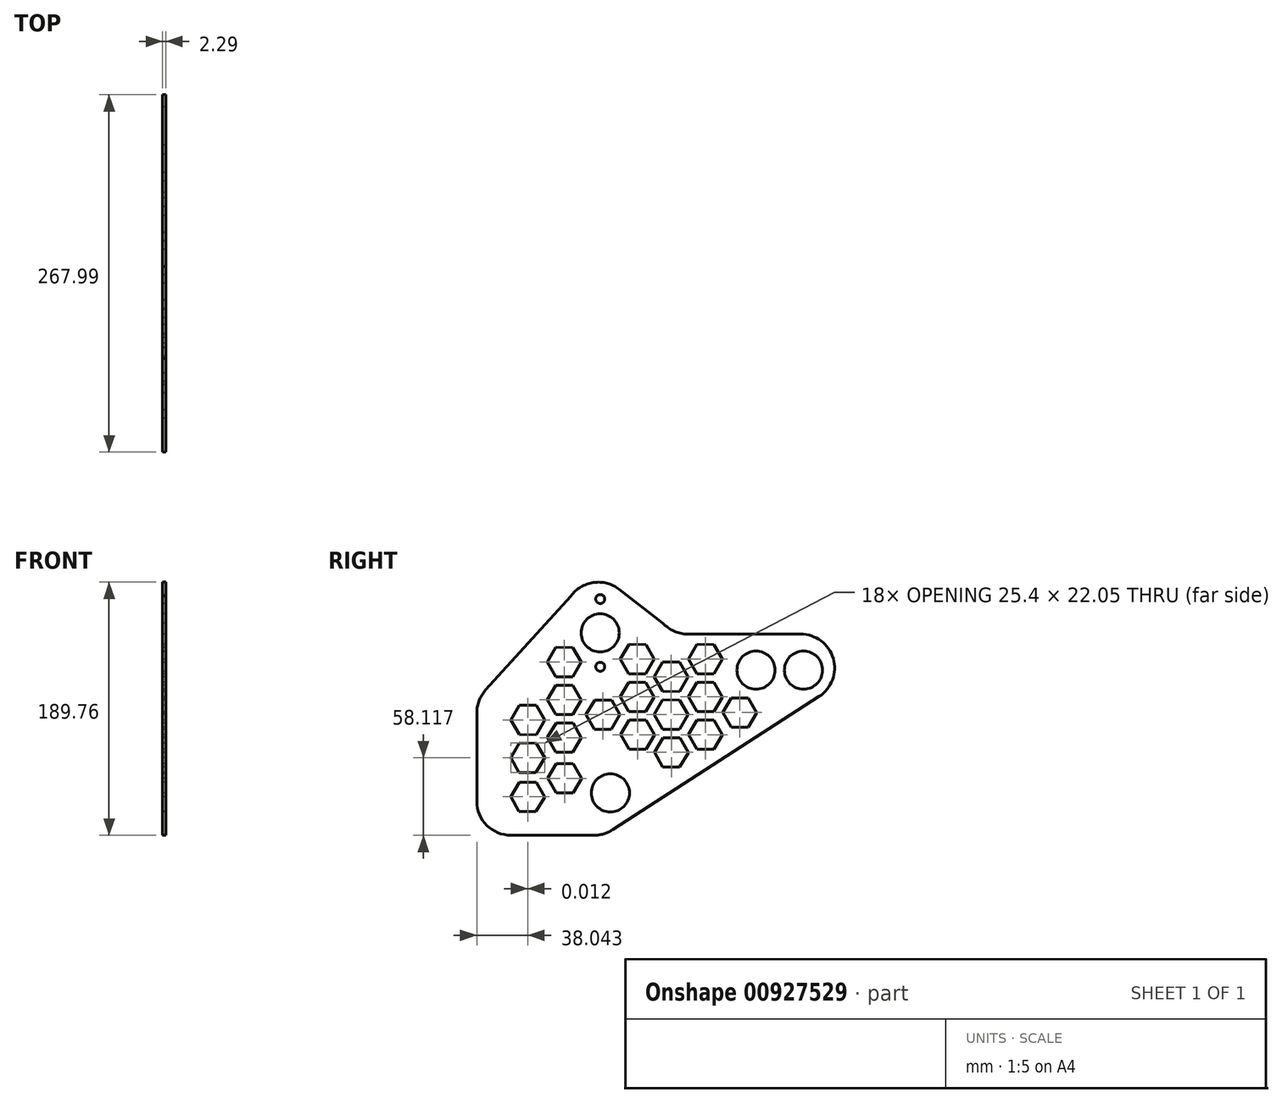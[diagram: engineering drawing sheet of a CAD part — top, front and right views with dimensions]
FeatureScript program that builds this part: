
annotation { "Feature Type Name" : "Feature", "Feature Type Description" : "" }
export const myFeature = defineFeature(function(context is Context, id is Id, definition is map)
    precondition{}
    {
        {
            var Q0;
            Q0=qCreatedBy(makeId("Right.planeOp"),FACE);
            var sketch = newSketch(context, id + "F0", { "sketchPlane" : qUnion([Q0])});
            skCircle(sketch, "E0", {"center": v(115.22, 53.73) * mm, "radius": 14.29 * mm});
            skCircle(sketch, "E1", {"center": v(79.66, 53.73) * mm, "radius": 14.29 * mm});
            skCircle(sketch, "E2", {"center": v(-37.05, 81.65) * mm, "radius": 14.29 * mm});
            skCircle(sketch, "E3", {"center": v(-29.41, -38.35) * mm, "radius": 14.29 * mm});
            skLineSegment(sketch, "E4", {"start": v(179.97, -95.5) * mm, "end": v(-160.98, -95.5) * mm});
            skCircle(sketch, "E5", {"center": v(-37.05, 107.05) * mm, "radius": 3.37 * mm});
            skCircle(sketch, "E6", {"center": v(-37.05, 56.25) * mm, "radius": 3.37 * mm});
            skLineSegment(sketch, "E7", {"start": v(-27.9, -66.03) * mm, "end": v(126.93, 33.98) * mm});
            skLineSegment(sketch, "E8", {"start": v(28.64, 80.72) * mm, "end": v(113.15, 80.72) * mm});
            skPoint(sketch, "E9.visualSharp", {"position": v(199.28, 80.72) * mm});
            skArc(sketch, "E9.filletArc", {"start": v(126.93, 33.98) * mm, "mid": v(137.51, 62.5) * mm, "end": v(113.15, 80.72) * mm});
            skPoint(sketch, "E10.visualSharp", {"position": v(17.39, 80.72) * mm});
            skArc(sketch, "E10.filletArc", {"start": v(9.83, 89.05) * mm, "mid": v(18.35, 82.9) * mm, "end": v(28.64, 80.72) * mm});
            skPoint(sketch, "E11.visualSharp", {"position": v(-180.09, -142.09) * mm});
            skPoint(sketch, "E12.visualSharp", {"position": v(-115.75, -108.8) * mm});
            skPoint(sketch, "E13.visualSharp", {"position": v(-31.87, -68.6) * mm});
            skCircle(sketch, "E14.cCircle", {"center": v(41.75, 62) * mm, "radius": 11 * mm, "construction": true});
            skLineSegment(sketch, "E14.0", {"start": v(35.35, 51.04) * mm, "end": v(29.05, 62.07) * mm});
            skLineSegment(sketch, "E14.1", {"start": v(29.05, 62.07) * mm, "end": v(35.45, 73.04) * mm});
            skLineSegment(sketch, "E14.2", {"start": v(35.45, 73.04) * mm, "end": v(48.15, 72.98) * mm});
            skLineSegment(sketch, "E14.3", {"start": v(48.15, 72.98) * mm, "end": v(54.45, 61.95) * mm});
            skLineSegment(sketch, "E14.4", {"start": v(54.45, 61.95) * mm, "end": v(48.05, 50.98) * mm});
            skLineSegment(sketch, "E14.5", {"start": v(48.05, 50.98) * mm, "end": v(35.35, 51.04) * mm});
            skPoint(sketch, "E14.0.midPoint", {"position": v(32.2, 56.55) * mm});
            skCircle(sketch, "E15.cCircle", {"center": v(41.69, 33.66) * mm, "radius": 11 * mm, "construction": true});
            skLineSegment(sketch, "E15.0", {"start": v(35.29, 22.7) * mm, "end": v(28.99, 33.72) * mm});
            skLineSegment(sketch, "E15.1", {"start": v(28.99, 33.72) * mm, "end": v(35.39, 44.69) * mm});
            skLineSegment(sketch, "E15.2", {"start": v(35.39, 44.69) * mm, "end": v(48.09, 44.63) * mm});
            skLineSegment(sketch, "E15.3", {"start": v(48.09, 44.63) * mm, "end": v(54.39, 33.6) * mm});
            skLineSegment(sketch, "E15.4", {"start": v(54.39, 33.6) * mm, "end": v(47.99, 22.64) * mm});
            skLineSegment(sketch, "E15.5", {"start": v(47.99, 22.64) * mm, "end": v(35.29, 22.7) * mm});
            skPoint(sketch, "E15.0.midPoint", {"position": v(32.14, 28.2) * mm});
            skCircle(sketch, "E16.cCircle", {"center": v(41.84, 5.32) * mm, "radius": 11 * mm, "construction": true});
            skLineSegment(sketch, "E16.0", {"start": v(35.45, -5.65) * mm, "end": v(29.14, 5.37) * mm});
            skLineSegment(sketch, "E16.1", {"start": v(29.14, 5.37) * mm, "end": v(35.54, 16.34) * mm});
            skLineSegment(sketch, "E16.2", {"start": v(35.54, 16.34) * mm, "end": v(48.24, 16.29) * mm});
            skLineSegment(sketch, "E16.3", {"start": v(48.24, 16.29) * mm, "end": v(54.54, 5.26) * mm});
            skLineSegment(sketch, "E16.4", {"start": v(54.54, 5.26) * mm, "end": v(48.15, -5.71) * mm});
            skLineSegment(sketch, "E16.5", {"start": v(48.15, -5.71) * mm, "end": v(35.45, -5.65) * mm});
            skPoint(sketch, "E16.0.midPoint", {"position": v(32.3, -0.14) * mm});
            skCircle(sketch, "E17.cCircle", {"center": v(16.13, 48.74) * mm, "radius": 11 * mm, "construction": true});
            skLineSegment(sketch, "E17.0", {"start": v(9.73, 37.77) * mm, "end": v(3.43, 48.8) * mm});
            skLineSegment(sketch, "E17.1", {"start": v(3.43, 48.8) * mm, "end": v(9.83, 59.77) * mm});
            skLineSegment(sketch, "E17.2", {"start": v(9.83, 59.77) * mm, "end": v(22.53, 59.71) * mm});
            skLineSegment(sketch, "E17.3", {"start": v(22.53, 59.71) * mm, "end": v(28.83, 48.69) * mm});
            skLineSegment(sketch, "E17.4", {"start": v(28.83, 48.69) * mm, "end": v(22.43, 37.72) * mm});
            skLineSegment(sketch, "E17.5", {"start": v(22.43, 37.72) * mm, "end": v(9.73, 37.77) * mm});
            skPoint(sketch, "E17.0.midPoint", {"position": v(6.58, 43.29) * mm});
            skCircle(sketch, "E18.cCircle", {"center": v(16.07, 20.4) * mm, "radius": 11 * mm, "construction": true});
            skLineSegment(sketch, "E18.0", {"start": v(9.67, 9.43) * mm, "end": v(3.37, 20.45) * mm});
            skLineSegment(sketch, "E18.1", {"start": v(3.37, 20.45) * mm, "end": v(9.77, 31.42) * mm});
            skLineSegment(sketch, "E18.2", {"start": v(9.77, 31.42) * mm, "end": v(22.47, 31.37) * mm});
            skLineSegment(sketch, "E18.3", {"start": v(22.47, 31.37) * mm, "end": v(28.77, 20.34) * mm});
            skLineSegment(sketch, "E18.4", {"start": v(28.77, 20.34) * mm, "end": v(22.37, 9.37) * mm});
            skLineSegment(sketch, "E18.5", {"start": v(22.37, 9.37) * mm, "end": v(9.67, 9.43) * mm});
            skPoint(sketch, "E18.0.midPoint", {"position": v(6.52, 14.94) * mm});
            skCircle(sketch, "E19.cCircle", {"center": v(16.23, -7.95) * mm, "radius": 11 * mm, "construction": true});
            skLineSegment(sketch, "E19.0", {"start": v(9.83, -18.92) * mm, "end": v(3.53, -7.9) * mm});
            skLineSegment(sketch, "E19.1", {"start": v(3.53, -7.9) * mm, "end": v(9.92, 3.08) * mm});
            skLineSegment(sketch, "E19.2", {"start": v(9.92, 3.08) * mm, "end": v(22.62, 3.02) * mm});
            skLineSegment(sketch, "E19.3", {"start": v(22.62, 3.02) * mm, "end": v(28.93, -8) * mm});
            skLineSegment(sketch, "E19.4", {"start": v(28.93, -8) * mm, "end": v(22.53, -18.98) * mm});
            skLineSegment(sketch, "E19.5", {"start": v(22.53, -18.98) * mm, "end": v(9.83, -18.92) * mm});
            skPoint(sketch, "E19.0.midPoint", {"position": v(6.68, -13.4) * mm});
            skCircle(sketch, "E20.cCircle", {"center": v(-9.22, 62) * mm, "radius": 11 * mm, "construction": true});
            skLineSegment(sketch, "E20.0", {"start": v(-15.62, 51.04) * mm, "end": v(-21.92, 62.07) * mm});
            skLineSegment(sketch, "E20.1", {"start": v(-21.92, 62.07) * mm, "end": v(-15.52, 73.04) * mm});
            skLineSegment(sketch, "E20.2", {"start": v(-15.52, 73.04) * mm, "end": v(-2.82, 72.98) * mm});
            skLineSegment(sketch, "E20.3", {"start": v(-2.82, 72.98) * mm, "end": v(3.48, 61.95) * mm});
            skLineSegment(sketch, "E20.4", {"start": v(3.48, 61.95) * mm, "end": v(-2.92, 50.98) * mm});
            skLineSegment(sketch, "E20.5", {"start": v(-2.92, 50.98) * mm, "end": v(-15.62, 51.04) * mm});
            skPoint(sketch, "E20.0.midPoint", {"position": v(-18.77, 56.55) * mm});
            skCircle(sketch, "E21.cCircle", {"center": v(-9.27, 33.66) * mm, "radius": 11 * mm, "construction": true});
            skLineSegment(sketch, "E21.0", {"start": v(-15.67, 22.7) * mm, "end": v(-21.97, 33.72) * mm});
            skLineSegment(sketch, "E21.1", {"start": v(-21.97, 33.72) * mm, "end": v(-15.58, 44.69) * mm});
            skLineSegment(sketch, "E21.2", {"start": v(-15.58, 44.69) * mm, "end": v(-2.88, 44.63) * mm});
            skLineSegment(sketch, "E21.3", {"start": v(-2.88, 44.63) * mm, "end": v(3.43, 33.6) * mm});
            skLineSegment(sketch, "E21.4", {"start": v(3.43, 33.6) * mm, "end": v(-2.97, 22.64) * mm});
            skLineSegment(sketch, "E21.5", {"start": v(-2.97, 22.64) * mm, "end": v(-15.67, 22.7) * mm});
            skPoint(sketch, "E21.0.midPoint", {"position": v(-18.82, 28.2) * mm});
            skCircle(sketch, "E22.cCircle", {"center": v(-9.12, 5.32) * mm, "radius": 11 * mm, "construction": true});
            skLineSegment(sketch, "E22.0", {"start": v(-15.52, -5.65) * mm, "end": v(-21.82, 5.37) * mm});
            skLineSegment(sketch, "E22.1", {"start": v(-21.82, 5.37) * mm, "end": v(-15.42, 16.34) * mm});
            skLineSegment(sketch, "E22.2", {"start": v(-15.42, 16.34) * mm, "end": v(-2.72, 16.29) * mm});
            skLineSegment(sketch, "E22.3", {"start": v(-2.72, 16.29) * mm, "end": v(3.58, 5.26) * mm});
            skLineSegment(sketch, "E22.4", {"start": v(3.58, 5.26) * mm, "end": v(-2.82, -5.71) * mm});
            skLineSegment(sketch, "E22.5", {"start": v(-2.82, -5.71) * mm, "end": v(-15.52, -5.65) * mm});
            skPoint(sketch, "E22.0.midPoint", {"position": v(-18.67, -0.14) * mm});
            skCircle(sketch, "E23.cCircle", {"center": v(-34.94, 20.34) * mm, "radius": 11 * mm, "construction": true});
            skLineSegment(sketch, "E23.0", {"start": v(-41.34, 9.37) * mm, "end": v(-47.64, 20.4) * mm});
            skLineSegment(sketch, "E23.1", {"start": v(-47.64, 20.4) * mm, "end": v(-41.25, 31.37) * mm});
            skLineSegment(sketch, "E23.2", {"start": v(-41.25, 31.37) * mm, "end": v(-28.55, 31.31) * mm});
            skLineSegment(sketch, "E23.3", {"start": v(-28.55, 31.31) * mm, "end": v(-22.24, 20.28) * mm});
            skLineSegment(sketch, "E23.4", {"start": v(-22.24, 20.28) * mm, "end": v(-28.64, 9.31) * mm});
            skLineSegment(sketch, "E23.5", {"start": v(-28.64, 9.31) * mm, "end": v(-41.34, 9.37) * mm});
            skPoint(sketch, "E23.0.midPoint", {"position": v(-44.5, 14.88) * mm});
            skCircle(sketch, "E24.cCircle", {"center": v(-63.94, 59.77) * mm, "radius": 11 * mm, "construction": true});
            skLineSegment(sketch, "E24.0", {"start": v(-70.34, 48.8) * mm, "end": v(-76.64, 59.83) * mm});
            skLineSegment(sketch, "E24.1", {"start": v(-76.64, 59.83) * mm, "end": v(-70.24, 70.8) * mm});
            skLineSegment(sketch, "E24.2", {"start": v(-70.24, 70.8) * mm, "end": v(-57.54, 70.74) * mm});
            skLineSegment(sketch, "E24.3", {"start": v(-57.54, 70.74) * mm, "end": v(-51.24, 59.71) * mm});
            skLineSegment(sketch, "E24.4", {"start": v(-51.24, 59.71) * mm, "end": v(-57.64, 48.74) * mm});
            skLineSegment(sketch, "E24.5", {"start": v(-57.64, 48.74) * mm, "end": v(-70.34, 48.8) * mm});
            skPoint(sketch, "E24.0.midPoint", {"position": v(-73.5, 54.31) * mm});
            skCircle(sketch, "E25.cCircle", {"center": v(-64, 31.42) * mm, "radius": 11 * mm, "construction": true});
            skLineSegment(sketch, "E25.0", {"start": v(-70.4, 20.45) * mm, "end": v(-76.7, 31.48) * mm});
            skLineSegment(sketch, "E25.1", {"start": v(-76.7, 31.48) * mm, "end": v(-70.3, 42.45) * mm});
            skLineSegment(sketch, "E25.2", {"start": v(-70.3, 42.45) * mm, "end": v(-57.6, 42.4) * mm});
            skLineSegment(sketch, "E25.3", {"start": v(-57.6, 42.4) * mm, "end": v(-51.3, 31.37) * mm});
            skLineSegment(sketch, "E25.4", {"start": v(-51.3, 31.37) * mm, "end": v(-57.7, 20.4) * mm});
            skLineSegment(sketch, "E25.5", {"start": v(-57.7, 20.4) * mm, "end": v(-70.4, 20.45) * mm});
            skPoint(sketch, "E25.0.midPoint", {"position": v(-73.55, 25.97) * mm});
            skCircle(sketch, "E26.cCircle", {"center": v(-63.84, 3.08) * mm, "radius": 11 * mm, "construction": true});
            skLineSegment(sketch, "E26.0", {"start": v(-70.24, -7.9) * mm, "end": v(-76.54, 3.13) * mm});
            skLineSegment(sketch, "E26.1", {"start": v(-76.54, 3.13) * mm, "end": v(-70.15, 14.1) * mm});
            skLineSegment(sketch, "E26.2", {"start": v(-70.15, 14.1) * mm, "end": v(-57.45, 14.05) * mm});
            skLineSegment(sketch, "E26.3", {"start": v(-57.45, 14.05) * mm, "end": v(-51.15, 3.02) * mm});
            skLineSegment(sketch, "E26.4", {"start": v(-51.15, 3.02) * mm, "end": v(-57.54, -7.95) * mm});
            skLineSegment(sketch, "E26.5", {"start": v(-57.54, -7.95) * mm, "end": v(-70.24, -7.9) * mm});
            skPoint(sketch, "E26.0.midPoint", {"position": v(-73.4, -2.38) * mm});
            skCircle(sketch, "E27.cCircle", {"center": v(-91.34, 16.36) * mm, "radius": 11 * mm, "construction": true});
            skLineSegment(sketch, "E27.0", {"start": v(-97.74, 5.4) * mm, "end": v(-104.04, 16.42) * mm});
            skLineSegment(sketch, "E27.1", {"start": v(-104.04, 16.42) * mm, "end": v(-97.64, 27.4) * mm});
            skLineSegment(sketch, "E27.2", {"start": v(-97.64, 27.4) * mm, "end": v(-84.94, 27.33) * mm});
            skLineSegment(sketch, "E27.3", {"start": v(-84.94, 27.33) * mm, "end": v(-78.64, 16.3) * mm});
            skLineSegment(sketch, "E27.4", {"start": v(-78.64, 16.3) * mm, "end": v(-85.04, 5.34) * mm});
            skLineSegment(sketch, "E27.5", {"start": v(-85.04, 5.34) * mm, "end": v(-97.74, 5.4) * mm});
            skPoint(sketch, "E27.0.midPoint", {"position": v(-100.89, 10.9) * mm});
            skCircle(sketch, "E28.cCircle", {"center": v(-91.4, -11.98) * mm, "radius": 11 * mm, "construction": true});
            skLineSegment(sketch, "E28.0", {"start": v(-97.8, -22.95) * mm, "end": v(-104.1, -11.93) * mm});
            skLineSegment(sketch, "E28.1", {"start": v(-104.1, -11.93) * mm, "end": v(-97.7, -0.96) * mm});
            skLineSegment(sketch, "E28.2", {"start": v(-97.7, -0.96) * mm, "end": v(-85, -1.01) * mm});
            skLineSegment(sketch, "E28.3", {"start": v(-85, -1.01) * mm, "end": v(-78.7, -12.04) * mm});
            skLineSegment(sketch, "E28.4", {"start": v(-78.7, -12.04) * mm, "end": v(-85.1, -23.01) * mm});
            skLineSegment(sketch, "E28.5", {"start": v(-85.1, -23.01) * mm, "end": v(-97.8, -22.95) * mm});
            skPoint(sketch, "E28.0.midPoint", {"position": v(-100.95, -17.44) * mm});
            skPoint(sketch, "E29.0.midPoint", {"position": v(-18.57, -28.27) * mm});
            skCircle(sketch, "E30.cCircle", {"center": v(67.55, 21.88) * mm, "radius": 11 * mm, "construction": true});
            skLineSegment(sketch, "E30.0", {"start": v(61.15, 10.9) * mm, "end": v(54.85, 21.93) * mm});
            skLineSegment(sketch, "E30.1", {"start": v(54.85, 21.93) * mm, "end": v(61.25, 32.9) * mm});
            skLineSegment(sketch, "E30.2", {"start": v(61.25, 32.9) * mm, "end": v(73.95, 32.85) * mm});
            skLineSegment(sketch, "E30.3", {"start": v(73.95, 32.85) * mm, "end": v(80.25, 21.82) * mm});
            skLineSegment(sketch, "E30.4", {"start": v(80.25, 21.82) * mm, "end": v(73.85, 10.85) * mm});
            skLineSegment(sketch, "E30.5", {"start": v(73.85, 10.85) * mm, "end": v(61.15, 10.9) * mm});
            skPoint(sketch, "E30.0.midPoint", {"position": v(58, 16.42) * mm});
            skLineSegment(sketch, "E31", {"start": v(9.83, 89.05) * mm, "end": v(-22.94, 114.36) * mm});
            skPoint(sketch, "E32.visualSharp", {"position": v(-43.65, 130.36) * mm});
            skArc(sketch, "E32.filletArc", {"start": v(-22.94, 114.36) * mm, "mid": v(-42.08, 119.4) * mm, "end": v(-59.02, 109.2) * mm});
            skPoint(sketch, "E33.visualSharp", {"position": v(-120.3, -70.1) * mm});
            skPoint(sketch, "E34.visualSharp", {"position": v(-120.3, 24.83) * mm});
            skLineSegment(sketch, "E35", {"start": v(9.83, 89.05) * mm, "end": v(-59.02, 142.24) * mm});
            skLineSegment(sketch, "E36", {"start": v(-41.68, -70.1) * mm, "end": v(-104.04, -70.1) * mm});
            skLineSegment(sketch, "E37", {"start": v(-129.44, 21.7) * mm, "end": v(-129.44, -44.7) * mm});
            skLineSegment(sketch, "E38", {"start": v(-59.02, 109.2) * mm, "end": v(-122.86, 38.76) * mm});
            skPoint(sketch, "E39.visualSharp", {"position": v(-129.44, 31.5) * mm});
            skArc(sketch, "E39.filletArc", {"start": v(-122.86, 38.76) * mm, "mid": v(-127.74, 30.85) * mm, "end": v(-129.44, 21.7) * mm});
            skPoint(sketch, "E40.visualSharp", {"position": v(-129.44, -70.1) * mm});
            skArc(sketch, "E40.filletArc", {"start": v(-129.44, -44.7) * mm, "mid": v(-122, -62.66) * mm, "end": v(-104.04, -70.1) * mm});
            skPoint(sketch, "E41.visualSharp", {"position": v(-34.19, -70.1) * mm});
            skArc(sketch, "E41.filletArc", {"start": v(-41.68, -70.1) * mm, "mid": v(-34.5, -69.06) * mm, "end": v(-27.9, -66.03) * mm});
            skCircle(sketch, "E42.cCircle", {"center": v(-63.75, -27.38) * mm, "radius": 11 * mm, "construction": true});
            skLineSegment(sketch, "E42.0", {"start": v(-70.15, -38.35) * mm, "end": v(-76.45, -27.32) * mm});
            skLineSegment(sketch, "E42.1", {"start": v(-76.45, -27.32) * mm, "end": v(-70.05, -16.35) * mm});
            skLineSegment(sketch, "E42.2", {"start": v(-70.05, -16.35) * mm, "end": v(-57.35, -16.4) * mm});
            skLineSegment(sketch, "E42.3", {"start": v(-57.35, -16.4) * mm, "end": v(-51.05, -27.43) * mm});
            skLineSegment(sketch, "E42.4", {"start": v(-51.05, -27.43) * mm, "end": v(-57.45, -38.4) * mm});
            skLineSegment(sketch, "E42.5", {"start": v(-57.45, -38.4) * mm, "end": v(-70.15, -38.35) * mm});
            skPoint(sketch, "E42.0.midPoint", {"position": v(-73.3, -32.83) * mm});
            skCircle(sketch, "E43.cCircle", {"center": v(-91.39, -41.32) * mm, "radius": 11 * mm, "construction": true});
            skLineSegment(sketch, "E43.0", {"start": v(-97.78, -52.29) * mm, "end": v(-104.09, -41.26) * mm});
            skLineSegment(sketch, "E43.1", {"start": v(-104.09, -41.26) * mm, "end": v(-97.69, -30.3) * mm});
            skLineSegment(sketch, "E43.2", {"start": v(-97.69, -30.3) * mm, "end": v(-84.99, -30.35) * mm});
            skLineSegment(sketch, "E43.3", {"start": v(-84.99, -30.35) * mm, "end": v(-78.69, -41.37) * mm});
            skLineSegment(sketch, "E43.4", {"start": v(-78.69, -41.37) * mm, "end": v(-85.08, -52.34) * mm});
            skLineSegment(sketch, "E43.5", {"start": v(-85.08, -52.34) * mm, "end": v(-97.78, -52.29) * mm});
            skPoint(sketch, "E43.0.midPoint", {"position": v(-100.93, -46.77) * mm});
            skSolve(sketch);
        }
        {
            var Q0;
            Q0=makeQuery(id+"F0.imprint","IMPRINT",FACE,{"disambiguationData":[TD([[makeQuery(id+"F0.imprint","IMPRINT",EDGE,{"derivedFrom":sQuery(id+"F0.wireOp",EDGE,"E0")}),-1.0]])]});
            extrude(context, id + "F1", {"entities" : qUnion([Q0]), "depth" : 2.3 * mm, "offsetDistance" : 25.4 * mm});
        }
    });
